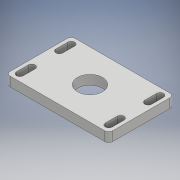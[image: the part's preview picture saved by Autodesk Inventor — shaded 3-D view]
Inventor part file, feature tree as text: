
AUTODESK INVENTOR PART (.ipt)
format: ipt  version: 2017 (Build 210142000, 142)  size: 138,752 bytes
history: native  units: mm
features: extrude x1, fillet x1, sketch x1
ambient origin geometry x8: Origin, YZ Plane, XZ Plane, XY Plane, X Axis, Y Axis, Z Axis, Center Point
bodies: Solid1 (feature_tree)
feature tree (3):
  extrude  "Extrusion1"  Depth=2.0mm
  fillet  "Fillet1"  Radius=3.5mm
  sketch  "Sketch1"  dims[d0=45.0mm d1=20.0mm d2=3.5mm d3=6.0mm d4=52.0mm d5=33.0mm d6=12.7mm d7=4.7625mm d8=0.0mm d9=2.0mm]
